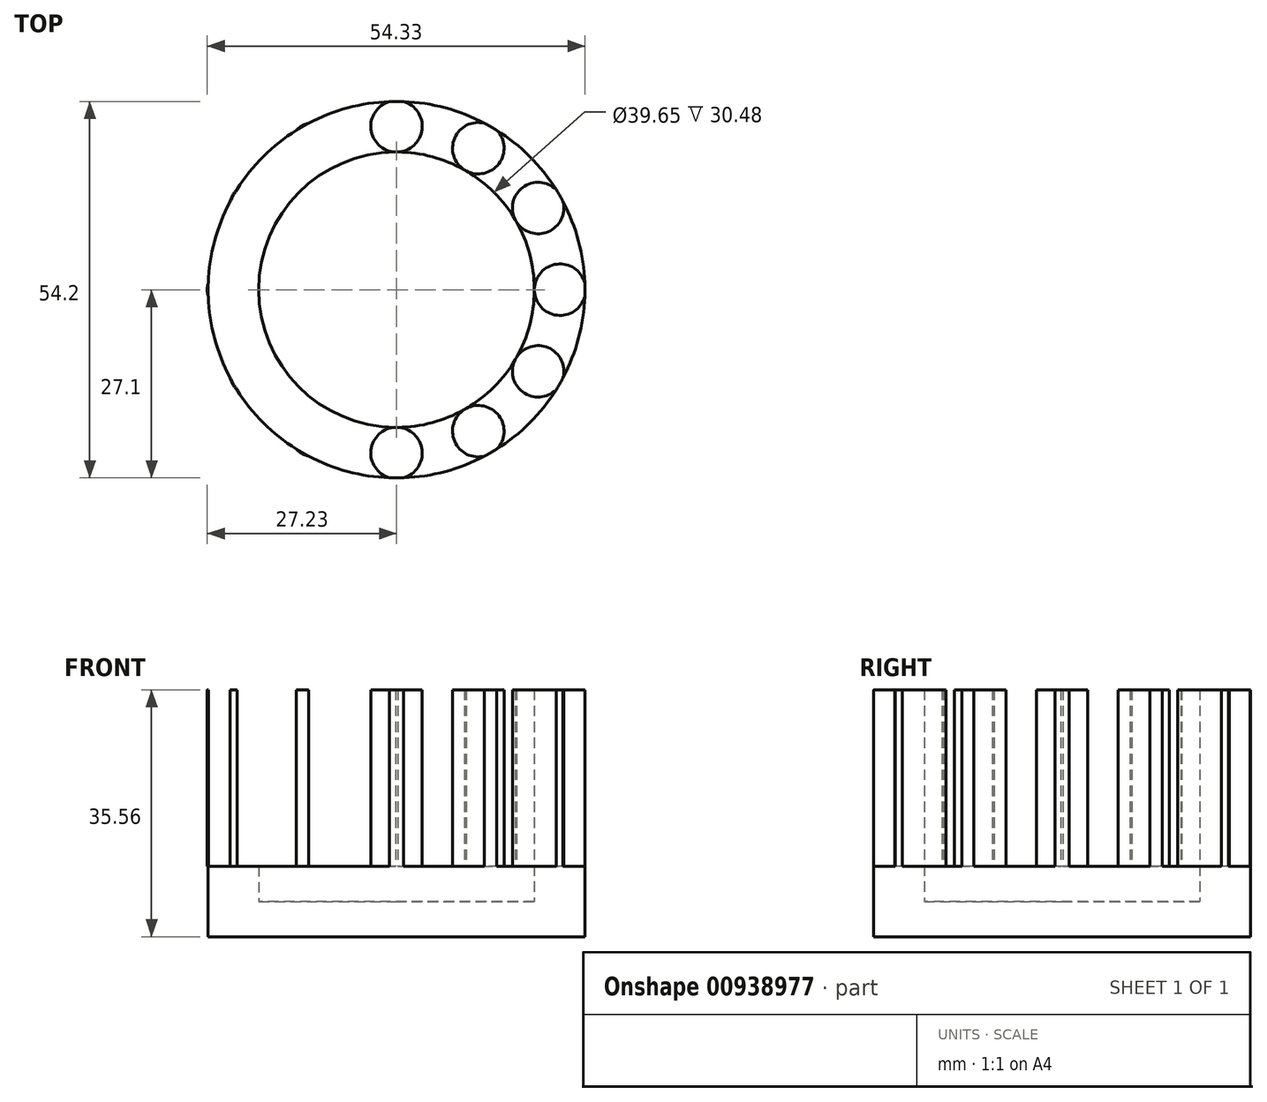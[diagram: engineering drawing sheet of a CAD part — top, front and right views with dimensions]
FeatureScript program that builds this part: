
annotation { "Feature Type Name" : "Feature", "Feature Type Description" : "" }
export const myFeature = defineFeature(function(context is Context, id is Id, definition is map)
    precondition{}
    {
        {
            var Q0;
            Q0=qCreatedBy(makeId("Top.planeOp"),FACE);
            var sketch = newSketch(context, id + "F0", { "sketchPlane" : qUnion([Q0])});
            skCircle(sketch, "E0", {"center": v(0, 0) * mm, "radius": 19.82 * mm});
            skCircle(sketch, "E1", {"center": v(0, 0) * mm, "radius": 27.1 * mm});
            skSolve(sketch);
        }
        {
            var Q0;
            Q0=makeQuery(id+"F0.imprint","IMPRINT",FACE,{"disambiguationData":[TD([[makeQuery(id+"F0.imprint","IMPRINT",EDGE,{"derivedFrom":sQuery(id+"F0.wireOp",EDGE,"E0")}),1.0]])]});
            extrude(context, id + "F1", {"entities" : qUnion([Q0]), "depth" : 5.08 * mm, "offsetDistance" : 25.4 * mm});
        }
        {
            var Q0;
            Q0=makeQuery(id+"F0.imprint","IMPRINT",FACE,{"disambiguationData":[TD([[makeQuery(id+"F0.imprint","IMPRINT",EDGE,{"derivedFrom":sQuery(id+"F0.wireOp",EDGE,"E0")}),-1.0]])]});
            extrude(context, id + "F2", {"entities" : qUnion([Q0]), "operationType" : NewBodyOperationType.ADD, "depth" : 10.16 * mm, "offsetDistance" : 25.4 * mm});
        }
        {
            var Q0;
            Q0=makeQuery(id+"F2.opExtrude","CAP_FACE",FACE,{"disambiguationData":[OSD([sQuery(id+"F0.wireOp",EDGE,"E0"),sQuery(id+"F0.wireOp",EDGE,"E1")])],"isStart":false});
            var sketch = newSketch(context, id + "F3", { "sketchPlane" : qUnion([Q0])});
            skCircle(sketch, "E2", {"center": v(23.52, 0) * mm, "radius": 3.7 * mm});
            skCircle(sketch, "E3.1.0", {"center": v(20.37, 11.76) * mm, "radius": 3.7 * mm});
            skCircle(sketch, "E3.2.0", {"center": v(11.76, 20.37) * mm, "radius": 3.7 * mm});
            skCircle(sketch, "E3.3.0", {"center": v(0, 23.52) * mm, "radius": 3.7 * mm});
            skCircle(sketch, "E3.4.0", {"center": v(-11.76, 20.37) * mm, "radius": 3.7 * mm});
            skCircle(sketch, "E3.5.0", {"center": v(-20.37, 11.76) * mm, "radius": 3.7 * mm});
            skCircle(sketch, "E3.6.0", {"center": v(-23.52, 0) * mm, "radius": 3.7 * mm});
            skCircle(sketch, "E3.7.0", {"center": v(-20.37, -11.76) * mm, "radius": 3.7 * mm});
            skCircle(sketch, "E3.8.0", {"center": v(-11.76, -20.37) * mm, "radius": 3.7 * mm});
            skCircle(sketch, "E3.9.0", {"center": v(0, -23.52) * mm, "radius": 3.7 * mm});
            skCircle(sketch, "E3.10.0", {"center": v(11.76, -20.37) * mm, "radius": 3.7 * mm});
            skCircle(sketch, "E3.11.0", {"center": v(20.37, -11.76) * mm, "radius": 3.7 * mm});
            skPoint(sketch, "E3.center", {"position": v(0, 0) * mm});
            skSolve(sketch);
        }
        {
            var Q0;
            {var subQ0=sQuery(id+"F3.wireOp",EDGE,"E3.5.0");var subQ1=makeQuery(id+"F2.opExtrude","CAP_EDGE",EDGE,{"disambiguationData":[OSD([sQuery(id+"F0.wireOp",EDGE,"E1")])],"isStart":false});var subQ2=makeQuery(id+"F3.imprint","INTERSECT",VERTEX,{"disambiguationData":[OD(0.0)],"derivedFrom":[subQ1,subQ0]});Q0=makeQuery(id+"F3.imprint","IMPRINT",FACE,{"disambiguationData":[TD([[makeQuery(id+"F3.imprint","IMPRINT",EDGE,{"disambiguationData":[TD([[subQ2,-1.0]])],"derivedFrom":subQ0}),1.0]])]});}
            var Q1;
            {var subQ0=sQuery(id+"F3.wireOp",EDGE,"E3.6.0");var subQ1=makeQuery(id+"F2.opExtrude","CAP_EDGE",EDGE,{"disambiguationData":[OSD([sQuery(id+"F0.wireOp",EDGE,"E1")])],"isStart":false});var subQ2=makeQuery(id+"F3.imprint","INTERSECT",VERTEX,{"disambiguationData":[OD(0.0)],"derivedFrom":[subQ1,subQ0]});Q1=makeQuery(id+"F3.imprint","IMPRINT",FACE,{"disambiguationData":[TD([[makeQuery(id+"F3.imprint","IMPRINT",EDGE,{"disambiguationData":[TD([[subQ2,-1.0]])],"derivedFrom":subQ0}),1.0]])]});}
            var Q2;
            {var subQ0=sQuery(id+"F3.wireOp",EDGE,"E3.7.0");var subQ1=makeQuery(id+"F2.opExtrude","CAP_EDGE",EDGE,{"disambiguationData":[OSD([sQuery(id+"F0.wireOp",EDGE,"E1")])],"isStart":false});var subQ2=makeQuery(id+"F3.imprint","INTERSECT",VERTEX,{"disambiguationData":[OD(0.0)],"derivedFrom":[subQ1,subQ0]});Q2=makeQuery(id+"F3.imprint","IMPRINT",FACE,{"disambiguationData":[TD([[makeQuery(id+"F3.imprint","IMPRINT",EDGE,{"disambiguationData":[TD([[subQ2,-1.0]])],"derivedFrom":subQ0}),1.0]])]});}
            var Q3;
            {var subQ0=sQuery(id+"F3.wireOp",EDGE,"E3.8.0");var subQ1=makeQuery(id+"F2.opExtrude","CAP_EDGE",EDGE,{"disambiguationData":[OSD([sQuery(id+"F0.wireOp",EDGE,"E1")])],"isStart":false});var subQ2=makeQuery(id+"F3.imprint","INTERSECT",VERTEX,{"disambiguationData":[OD(0.0)],"derivedFrom":[subQ1,subQ0]});Q3=makeQuery(id+"F3.imprint","IMPRINT",FACE,{"disambiguationData":[TD([[makeQuery(id+"F3.imprint","IMPRINT",EDGE,{"disambiguationData":[TD([[subQ2,-1.0]])],"derivedFrom":subQ0}),1.0]])]});}
            var Q4;
            {var subQ0=sQuery(id+"F3.wireOp",EDGE,"E3.9.0");var subQ1=makeQuery(id+"F2.opExtrude","CAP_EDGE",EDGE,{"disambiguationData":[OSD([sQuery(id+"F0.wireOp",EDGE,"E1")])],"isStart":false});var subQ2=makeQuery(id+"F3.imprint","INTERSECT",VERTEX,{"disambiguationData":[OD(0.0)],"derivedFrom":[subQ1,subQ0]});Q4=makeQuery(id+"F3.imprint","IMPRINT",FACE,{"disambiguationData":[TD([[makeQuery(id+"F3.imprint","IMPRINT",EDGE,{"disambiguationData":[TD([[subQ2,-1.0]])],"derivedFrom":subQ0}),1.0]])]});}
            var Q5;
            {var subQ0=sQuery(id+"F3.wireOp",EDGE,"E3.10.0");var subQ1=makeQuery(id+"F2.opExtrude","CAP_EDGE",EDGE,{"disambiguationData":[OSD([sQuery(id+"F0.wireOp",EDGE,"E1")])],"isStart":false});var subQ2=makeQuery(id+"F3.imprint","INTERSECT",VERTEX,{"disambiguationData":[OD(0.0)],"derivedFrom":[subQ1,subQ0]});Q5=makeQuery(id+"F3.imprint","IMPRINT",FACE,{"disambiguationData":[TD([[makeQuery(id+"F3.imprint","IMPRINT",EDGE,{"disambiguationData":[TD([[subQ2,-1.0]])],"derivedFrom":subQ0}),1.0]])]});}
            var Q6;
            {var subQ0=sQuery(id+"F3.wireOp",EDGE,"E3.4.0");var subQ1=makeQuery(id+"F2.opExtrude","CAP_EDGE",EDGE,{"disambiguationData":[OSD([sQuery(id+"F0.wireOp",EDGE,"E1")])],"isStart":false});var subQ2=makeQuery(id+"F3.imprint","INTERSECT",VERTEX,{"disambiguationData":[OD(0.0)],"derivedFrom":[subQ1,subQ0]});Q6=makeQuery(id+"F3.imprint","IMPRINT",FACE,{"disambiguationData":[TD([[makeQuery(id+"F3.imprint","IMPRINT",EDGE,{"disambiguationData":[TD([[subQ2,-1.0]])],"derivedFrom":subQ0}),1.0]])]});}
            var Q7;
            {var subQ0=sQuery(id+"F3.wireOp",EDGE,"E3.3.0");var subQ1=makeQuery(id+"F2.opExtrude","CAP_EDGE",EDGE,{"disambiguationData":[OSD([sQuery(id+"F0.wireOp",EDGE,"E1")])],"isStart":false});var subQ2=makeQuery(id+"F3.imprint","INTERSECT",VERTEX,{"disambiguationData":[OD(0.0)],"derivedFrom":[subQ1,subQ0]});Q7=makeQuery(id+"F3.imprint","IMPRINT",FACE,{"disambiguationData":[TD([[makeQuery(id+"F3.imprint","IMPRINT",EDGE,{"disambiguationData":[TD([[subQ2,-1.0]])],"derivedFrom":subQ0}),1.0]])]});}
            var Q8;
            {var subQ0=sQuery(id+"F3.wireOp",EDGE,"E3.2.0");var subQ1=makeQuery(id+"F2.opExtrude","CAP_EDGE",EDGE,{"disambiguationData":[OSD([sQuery(id+"F0.wireOp",EDGE,"E1")])],"isStart":false});var subQ2=makeQuery(id+"F3.imprint","INTERSECT",VERTEX,{"disambiguationData":[OD(0.0)],"derivedFrom":[subQ1,subQ0]});Q8=makeQuery(id+"F3.imprint","IMPRINT",FACE,{"disambiguationData":[TD([[makeQuery(id+"F3.imprint","IMPRINT",EDGE,{"disambiguationData":[TD([[subQ2,-1.0]])],"derivedFrom":subQ0}),1.0]])]});}
            var Q9;
            {var subQ0=sQuery(id+"F3.wireOp",EDGE,"E3.1.0");var subQ1=makeQuery(id+"F2.opExtrude","CAP_EDGE",EDGE,{"disambiguationData":[OSD([sQuery(id+"F0.wireOp",EDGE,"E1")])],"isStart":false});var subQ2=makeQuery(id+"F3.imprint","INTERSECT",VERTEX,{"disambiguationData":[OD(0.0)],"derivedFrom":[subQ1,subQ0]});Q9=makeQuery(id+"F3.imprint","IMPRINT",FACE,{"disambiguationData":[TD([[makeQuery(id+"F3.imprint","IMPRINT",EDGE,{"disambiguationData":[TD([[subQ2,-1.0]])],"derivedFrom":subQ0}),1.0]])]});}
            var Q10;
            {var subQ0=sQuery(id+"F3.wireOp",EDGE,"E2");var subQ1=makeQuery(id+"F2.opExtrude","CAP_EDGE",EDGE,{"disambiguationData":[OSD([sQuery(id+"F0.wireOp",EDGE,"E1")])],"isStart":false});var subQ2=makeQuery(id+"F3.imprint","INTERSECT",VERTEX,{"disambiguationData":[OD(0.0)],"derivedFrom":[subQ1,subQ0]});Q10=makeQuery(id+"F3.imprint","IMPRINT",FACE,{"disambiguationData":[TD([[makeQuery(id+"F3.imprint","IMPRINT",EDGE,{"disambiguationData":[TD([[subQ2,-1.0]])],"derivedFrom":subQ0}),1.0]])]});}
            var Q11;
            {var subQ0=sQuery(id+"F3.wireOp",EDGE,"E3.11.0");var subQ1=makeQuery(id+"F2.opExtrude","CAP_EDGE",EDGE,{"disambiguationData":[OSD([sQuery(id+"F0.wireOp",EDGE,"E1")])],"isStart":false});var subQ2=makeQuery(id+"F3.imprint","INTERSECT",VERTEX,{"disambiguationData":[OD(0.0)],"derivedFrom":[subQ1,subQ0]});Q11=makeQuery(id+"F3.imprint","IMPRINT",FACE,{"disambiguationData":[TD([[makeQuery(id+"F3.imprint","IMPRINT",EDGE,{"disambiguationData":[TD([[subQ2,-1.0]])],"derivedFrom":subQ0}),1.0]])]});}
            extrude(context, id + "F4", {"entities" : qUnion([Q0, Q1, Q2, Q3, Q4, Q5, Q6, Q7, Q8, Q9, Q10, Q11]), "operationType" : NewBodyOperationType.ADD, "depth" : 25.4 * mm, "offsetDistance" : 25.4 * mm});
        }
    });
